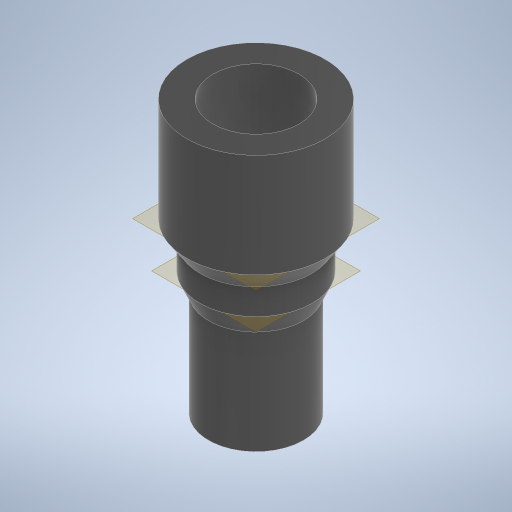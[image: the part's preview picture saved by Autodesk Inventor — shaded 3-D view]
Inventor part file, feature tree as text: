
AUTODESK INVENTOR PART (.ipt)
format: ipt  version: 2024 (Build 280153000, 153)  size: 266,240 bytes
history: native  units: mm
features: extrude x5, sketch x5, other x4, plane x2, loft x2
ambient origin geometry x8: Origin, YZ Plane, XZ Plane, XY Plane, X Axis, Y Axis, Z Axis, Center Point
bodies: Solid1 (feature_tree)
feature tree (18):
  extrude  "Extrusion1"  Depth=12.0mm TaperAngle=0.0deg
  extrude  "Extrusion2"  Depth=10.0mm TaperAngle=0.0deg
  plane  "Work Plane1"
  extrude  "Extrusion3"  Depth=13.0mm
  loft  "Loft1"
  plane  "Work Plane2"
  extrude  "Extrusion4"  Depth=10.0mm
  loft  "Loft2"
  extrude  "Extrusion5"  Depth=10.0mm TaperAngle=0.0deg
  sketch  "Sketch1"  dims[d0=11.0mm d1=12.0mm d2=0.0mm]
  sketch  "Sketch2"  dims[d3=6.0mm d4=10.0mm d5=0.0mm]
  sketch  "Sketch3"  dims[d6=2.25mm d7=13.0mm]
  other  "Edges1"
  other  "Edges2"
  sketch  "Sketch4"  dims[d8=3.0mm d9=0.0mm d10=0.0mm d11=90.0deg]
  other  "Edges3"
  other  "Edges4"
  sketch  "Sketch5"  dims[d12=0.0mm d13=90.0deg d14=2.25mm d15=16.0mm d16=12.0mm d17=0.0mm d18=0.0mm d19=90.0deg d20=0.0mm d21=90.0deg d22=10.0mm d23=10.0mm d24=0.0mm]
